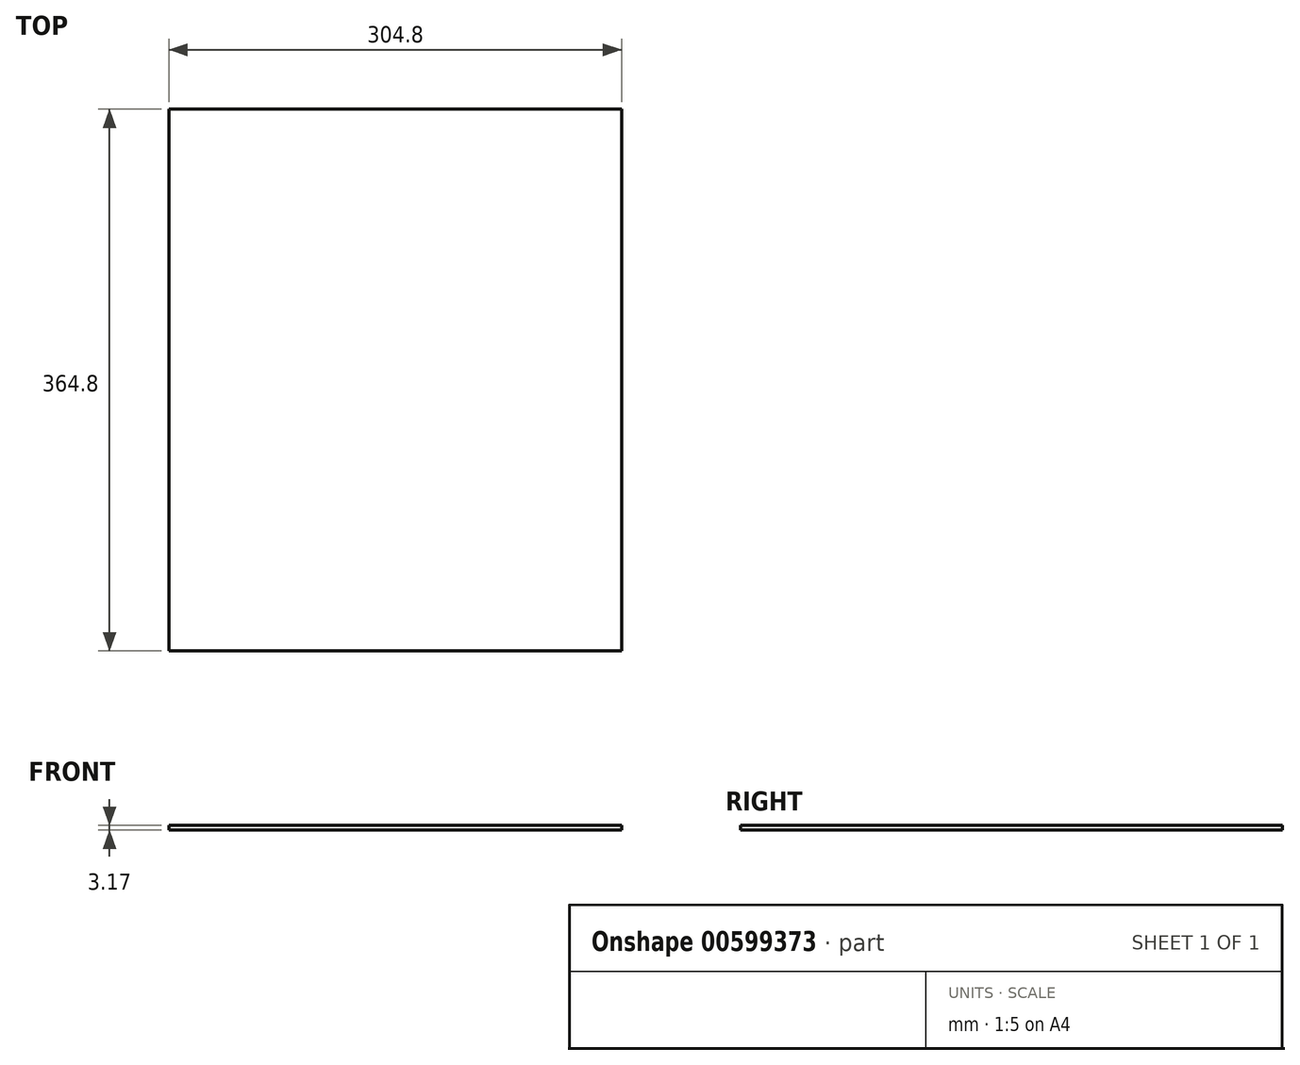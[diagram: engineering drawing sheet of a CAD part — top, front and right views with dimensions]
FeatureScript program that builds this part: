
annotation { "Feature Type Name" : "Feature", "Feature Type Description" : "" }
export const myFeature = defineFeature(function(context is Context, id is Id, definition is map)
    precondition{}
    {
        {
            var Q0;
            Q0=qCreatedBy(makeId("Top.planeOp"),FACE);
            var sketch = newSketch(context, id + "F0", { "sketchPlane" : qUnion([Q0])});
            skLineSegment(sketch, "E0.bottom", {"start": v(-152.4, 152.4) * mm, "end": v(152.4, 152.4) * mm});
            skLineSegment(sketch, "E0.top", {"start": v(-152.4, -152.4) * mm, "end": v(152.4, -152.4) * mm});
            skLineSegment(sketch, "E0.left", {"start": v(-152.4, 152.4) * mm, "end": v(-152.4, -152.4) * mm});
            skLineSegment(sketch, "E0.right", {"start": v(152.4, 152.4) * mm, "end": v(152.4, -152.4) * mm});
            skLineSegment(sketch, "E1.top", {"start": v(-152.4, 212.4) * mm, "end": v(152.4, 212.4) * mm});
            skLineSegment(sketch, "E1.left", {"start": v(-152.4, 152.4) * mm, "end": v(-152.4, 212.4) * mm});
            skLineSegment(sketch, "E1.right", {"start": v(152.4, 152.4) * mm, "end": v(152.4, 212.4) * mm});
            skSolve(sketch);
        }
        {
            var Q0;
            Q0=qSketchRegion(id+"F0",true);
            extrude(context, id + "F1", {"entities" : qUnion([Q0]), "depth" : 3.17 * mm});
        }
    });
